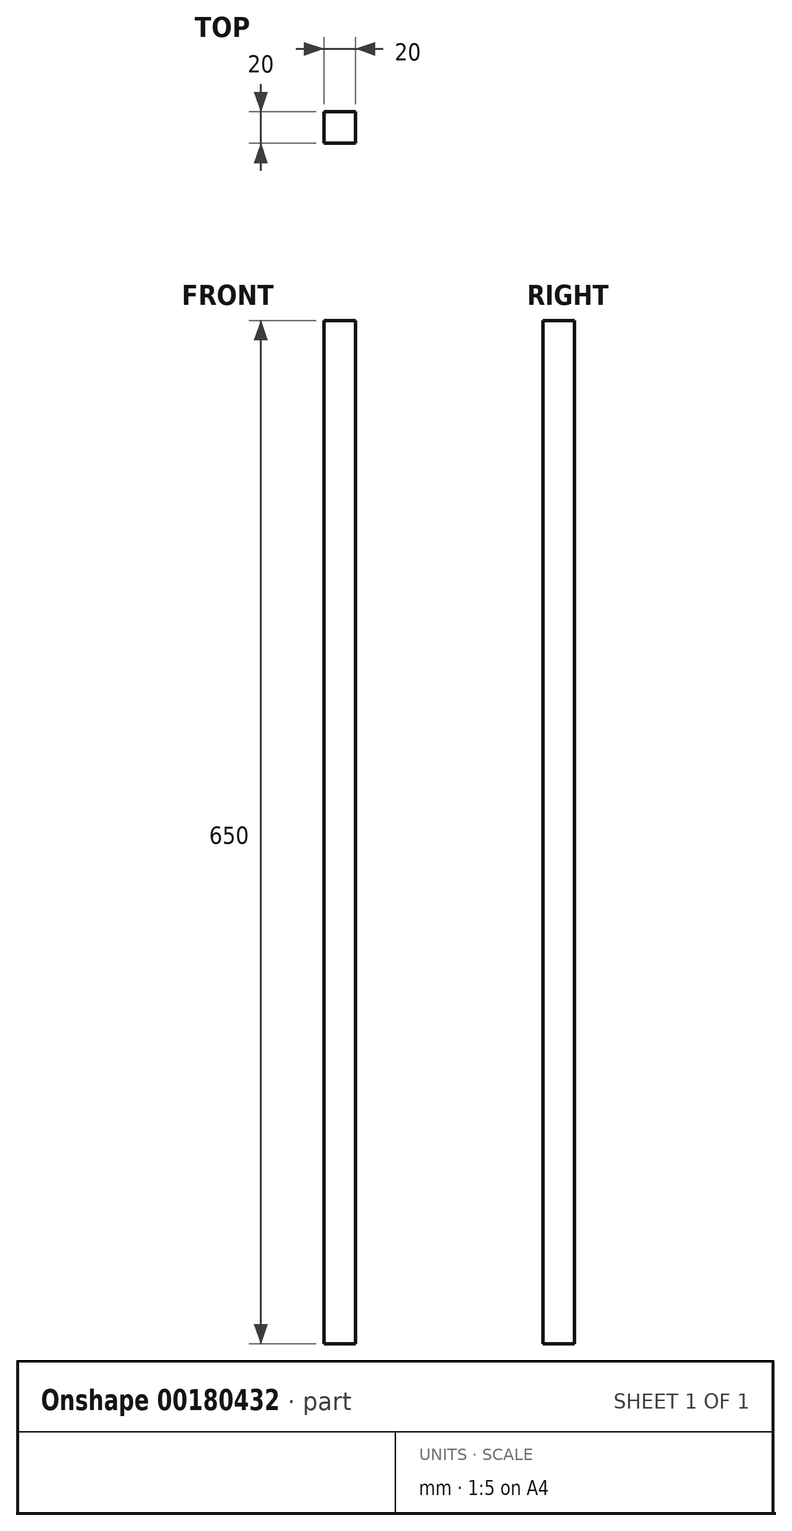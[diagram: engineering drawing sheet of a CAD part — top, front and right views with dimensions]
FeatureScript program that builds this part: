
annotation { "Feature Type Name" : "Feature", "Feature Type Description" : "" }
export const myFeature = defineFeature(function(context is Context, id is Id, definition is map)
    precondition{}
    {
        {
            var Q0;
            Q0=qCreatedBy(makeId("Top.planeOp"),FACE);
            var sketch = newSketch(context, id + "F0", { "sketchPlane" : qUnion([Q0])});
            skLineSegment(sketch, "E0.bottom", {"start": v(-84.62, -70.45) * mm, "end": v(-64.62, -70.45) * mm});
            skLineSegment(sketch, "E0.top", {"start": v(-84.62, -50.45) * mm, "end": v(-64.62, -50.45) * mm});
            skLineSegment(sketch, "E0.left", {"start": v(-84.62, -70.45) * mm, "end": v(-84.62, -50.45) * mm});
            skLineSegment(sketch, "E0.right", {"start": v(-64.62, -70.45) * mm, "end": v(-64.62, -50.45) * mm});
            skSolve(sketch);
        }
        {
            var Q0;
            Q0=makeQuery(id+"F0.imprint","IMPRINT",FACE,{"disambiguationData":[TD([[makeQuery(id+"F0.imprint","IMPRINT",EDGE,{"derivedFrom":sQuery(id+"F0.wireOp",EDGE,"E0.bottom")}),1.0]])]});
            extrude(context, id + "F1", {"entities" : qUnion([Q0]), "depth" : 650 * mm});
        }
    });
